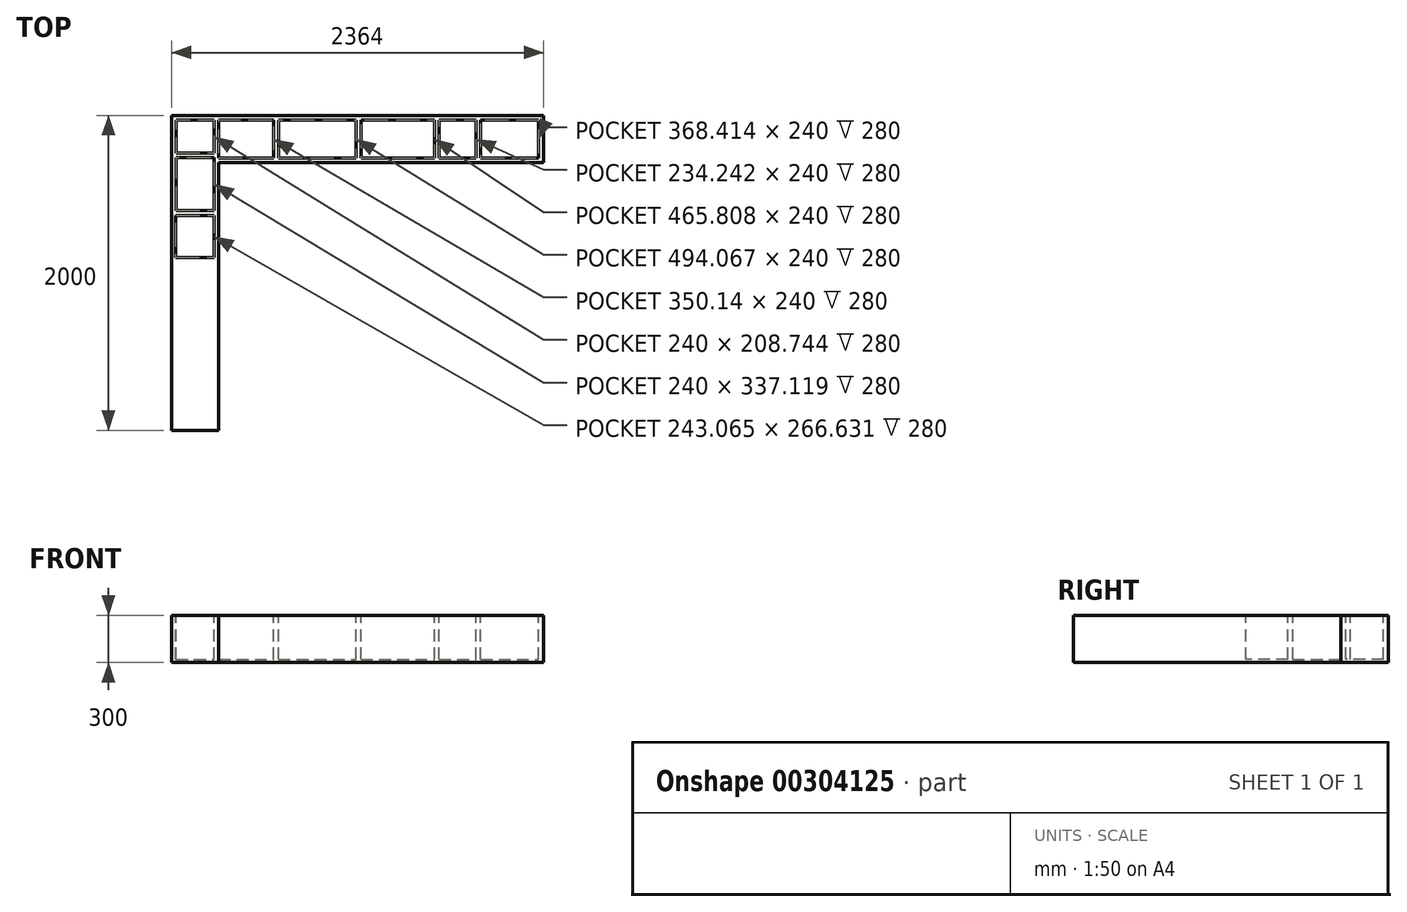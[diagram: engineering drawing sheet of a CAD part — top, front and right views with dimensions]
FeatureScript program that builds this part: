
annotation { "Feature Type Name" : "Feature", "Feature Type Description" : "" }
export const myFeature = defineFeature(function(context is Context, id is Id, definition is map)
    precondition{}
    {
        {
            var Q0;
            Q0=qCreatedBy(makeId("Top.planeOp"),FACE);
            var sketch = newSketch(context, id + "F0", { "sketchPlane" : qUnion([Q0])});
            skLineSegment(sketch, "E0.bottom", {"start": v(-1332.55, -1133.36) * mm, "end": v(-1032.55, -1133.36) * mm});
            skLineSegment(sketch, "E0.top", {"start": v(-1332.55, 866.64) * mm, "end": v(-1032.55, 866.64) * mm});
            skLineSegment(sketch, "E0.left", {"start": v(-1332.55, -1133.36) * mm, "end": v(-1332.55, 866.64) * mm});
            skLineSegment(sketch, "E0.right", {"start": v(-1032.55, -1133.36) * mm, "end": v(-1032.55, 866.64) * mm});
            skLineSegment(sketch, "E1.bottom", {"start": v(-1032.55, 866.64) * mm, "end": v(1031.45, 866.64) * mm});
            skLineSegment(sketch, "E1.top", {"start": v(-1032.55, 566.64) * mm, "end": v(1031.45, 566.64) * mm});
            skLineSegment(sketch, "E1.left", {"start": v(-1032.55, 866.64) * mm, "end": v(-1032.55, 566.64) * mm});
            skLineSegment(sketch, "E1.right", {"start": v(1031.45, 866.64) * mm, "end": v(1031.45, 566.64) * mm});
            skSolve(sketch);
        }
        {
            var Q0;
            Q0=makeQuery(id+"F0.imprint","IMPRINT",FACE,{"disambiguationData":[TD([[makeQuery(id+"F0.imprint","IMPRINT",EDGE,{"derivedFrom":sQuery(id+"F0.wireOp",EDGE,"E0.bottom")}),1.0]])]});
            var Q1;
            Q1=makeQuery(id+"F0.imprint","IMPRINT",FACE,{"disambiguationData":[TD([[makeQuery(id+"F0.imprint","IMPRINT",EDGE,{"derivedFrom":sQuery(id+"F0.wireOp",EDGE,"E1.bottom")}),-1.0]])]});
            extrude(context, id + "F1", {"entities" : qUnion([Q0, Q1]), "depth" : 300 * mm, "offsetDistance" : 25 * mm});
        }
        {
            var Q0;
            Q0=makeQuery(id+"F1.opExtrude","CAP_FACE",FACE,{"disambiguationData":[OSD([sQuery(id+"F0.wireOp",EDGE,"E0.bottom"),sQuery(id+"F0.wireOp",EDGE,"E0.top"),sQuery(id+"F0.wireOp",EDGE,"E0.left"),sQuery(id+"F0.wireOp",EDGE,"E0.right"),sQuery(id+"F0.wireOp",EDGE,"E1.bottom"),sQuery(id+"F0.wireOp",EDGE,"E1.top"),sQuery(id+"F0.wireOp",EDGE,"E1.right")])],"isStart":false});
            var sketch = newSketch(context, id + "F2", { "sketchPlane" : qUnion([Q0])});
            skLineSegment(sketch, "E2.bottom", {"start": v(-1305.62, 230.78) * mm, "end": v(-1062.55, 230.78) * mm});
            skLineSegment(sketch, "E2.top", {"start": v(-1305.62, -35.85) * mm, "end": v(-1062.55, -35.85) * mm});
            skLineSegment(sketch, "E2.left", {"start": v(-1305.62, 230.78) * mm, "end": v(-1305.62, -35.85) * mm});
            skLineSegment(sketch, "E2.right", {"start": v(-1062.55, 230.78) * mm, "end": v(-1062.55, -35.85) * mm});
            skLineSegment(sketch, "E3.bottom", {"start": v(-1062.55, 260.78) * mm, "end": v(-1302.55, 260.78) * mm});
            skLineSegment(sketch, "E3.top", {"start": v(-1062.55, 597.9) * mm, "end": v(-1302.55, 597.9) * mm});
            skLineSegment(sketch, "E3.left", {"start": v(-1062.55, 260.78) * mm, "end": v(-1062.55, 597.9) * mm});
            skLineSegment(sketch, "E3.right", {"start": v(-1302.55, 260.78) * mm, "end": v(-1302.55, 597.9) * mm});
            skLineSegment(sketch, "E4.bottom", {"start": v(-1302.55, 836.64) * mm, "end": v(-1062.55, 836.64) * mm});
            skLineSegment(sketch, "E4.top", {"start": v(-1302.55, 627.9) * mm, "end": v(-1062.55, 627.9) * mm});
            skLineSegment(sketch, "E4.left", {"start": v(-1302.55, 836.64) * mm, "end": v(-1302.55, 627.9) * mm});
            skLineSegment(sketch, "E4.right", {"start": v(-1062.55, 836.64) * mm, "end": v(-1062.55, 627.9) * mm});
            skLineSegment(sketch, "E5.top", {"start": v(-1032.55, 596.64) * mm, "end": v(-682.41, 596.64) * mm});
            skLineSegment(sketch, "E6.bottom", {"start": v(-652.41, 836.64) * mm, "end": v(-158.35, 836.64) * mm});
            skLineSegment(sketch, "E6.top", {"start": v(-652.41, 596.64) * mm, "end": v(-158.35, 596.64) * mm});
            skLineSegment(sketch, "E6.left", {"start": v(-652.41, 836.64) * mm, "end": v(-652.41, 596.64) * mm});
            skLineSegment(sketch, "E6.right", {"start": v(-158.35, 836.64) * mm, "end": v(-158.35, 596.64) * mm});
            skLineSegment(sketch, "E7.bottom", {"start": v(-128.35, 836.64) * mm, "end": v(337.46, 836.64) * mm});
            skLineSegment(sketch, "E7.top", {"start": v(-128.35, 596.64) * mm, "end": v(337.46, 596.64) * mm});
            skLineSegment(sketch, "E7.left", {"start": v(-128.35, 836.64) * mm, "end": v(-128.35, 596.64) * mm});
            skLineSegment(sketch, "E7.right", {"start": v(337.46, 836.64) * mm, "end": v(337.46, 596.64) * mm});
            skLineSegment(sketch, "E8.bottom", {"start": v(367.46, 836.64) * mm, "end": v(601.7, 836.64) * mm});
            skLineSegment(sketch, "E8.top", {"start": v(367.46, 596.64) * mm, "end": v(601.7, 596.64) * mm});
            skLineSegment(sketch, "E8.left", {"start": v(367.46, 836.64) * mm, "end": v(367.46, 596.64) * mm});
            skLineSegment(sketch, "E8.right", {"start": v(601.7, 836.64) * mm, "end": v(601.7, 596.64) * mm});
            skLineSegment(sketch, "E9.bottom", {"start": v(631.7, 836.64) * mm, "end": v(1000.12, 836.64) * mm});
            skLineSegment(sketch, "E9.top", {"start": v(631.7, 596.64) * mm, "end": v(1000.12, 596.64) * mm});
            skLineSegment(sketch, "E9.left", {"start": v(631.7, 836.64) * mm, "end": v(631.7, 596.64) * mm});
            skLineSegment(sketch, "E9.right", {"start": v(1000.12, 836.64) * mm, "end": v(1000.12, 596.64) * mm});
            skLineSegment(sketch, "E10", {"start": v(-1032.55, 596.64) * mm, "end": v(-1032.55, 836.64) * mm});
            skLineSegment(sketch, "E11", {"start": v(-1032.55, 836.64) * mm, "end": v(-682.41, 836.64) * mm});
            skLineSegment(sketch, "E12", {"start": v(-682.41, 836.64) * mm, "end": v(-682.41, 596.64) * mm});
            skSolve(sketch);
        }
        {
            var Q0;
            Q0=makeQuery(id+"F2.imprint","IMPRINT",FACE,{"disambiguationData":[TD([[makeQuery(id+"F2.imprint","IMPRINT",EDGE,{"derivedFrom":sQuery(id+"F2.wireOp",EDGE,"E2.bottom")}),-1.0]])]});
            var Q1;
            Q1=makeQuery(id+"F2.imprint","IMPRINT",FACE,{"disambiguationData":[TD([[makeQuery(id+"F2.imprint","IMPRINT",EDGE,{"derivedFrom":sQuery(id+"F2.wireOp",EDGE,"E3.bottom")}),-1.0]])]});
            var Q2;
            Q2=makeQuery(id+"F2.imprint","IMPRINT",FACE,{"disambiguationData":[TD([[makeQuery(id+"F2.imprint","IMPRINT",EDGE,{"derivedFrom":sQuery(id+"F2.wireOp",EDGE,"E4.bottom")}),-1.0]])]});
            var Q3;
            Q3=makeQuery(id+"F2.imprint","IMPRINT",FACE,{"disambiguationData":[TD([[makeQuery(id+"F2.imprint","IMPRINT",EDGE,{"derivedFrom":sQuery(id+"F2.wireOp",EDGE,"E5.top")}),1.0]])]});
            var Q4;
            Q4=makeQuery(id+"F2.imprint","IMPRINT",FACE,{"disambiguationData":[TD([[makeQuery(id+"F2.imprint","IMPRINT",EDGE,{"derivedFrom":sQuery(id+"F2.wireOp",EDGE,"E6.bottom")}),-1.0]])]});
            var Q5;
            Q5=makeQuery(id+"F2.imprint","IMPRINT",FACE,{"disambiguationData":[TD([[makeQuery(id+"F2.imprint","IMPRINT",EDGE,{"derivedFrom":sQuery(id+"F2.wireOp",EDGE,"E7.bottom")}),-1.0]])]});
            var Q6;
            Q6=makeQuery(id+"F2.imprint","IMPRINT",FACE,{"disambiguationData":[TD([[makeQuery(id+"F2.imprint","IMPRINT",EDGE,{"derivedFrom":sQuery(id+"F2.wireOp",EDGE,"E8.bottom")}),-1.0]])]});
            var Q7;
            Q7=makeQuery(id+"F2.imprint","IMPRINT",FACE,{"disambiguationData":[TD([[makeQuery(id+"F2.imprint","IMPRINT",EDGE,{"derivedFrom":sQuery(id+"F2.wireOp",EDGE,"E9.bottom")}),-1.0]])]});
            var Q8;
            Q8=makeQuery(id+"F2.imprint","IMPRINT",FACE,{"disambiguationData":[TD([[makeQuery(id+"F2.imprint","IMPRINT",EDGE,{"derivedFrom":sQuery(id+"F2.wireOp",EDGE,"f1vktL2T-XDao-MCao-i2m5-WC2OeJWGSlmK.bottom")}),-1.0]])]});
            extrude(context, id + "F3", {"entities" : qUnion([Q0, Q1, Q2, Q3, Q4, Q5, Q6, Q7, Q8]), "operationType" : NewBodyOperationType.REMOVE, "oppositeDirection" : true, "depth" : 280 * mm, "offsetDistance" : 25 * mm});
        }
    });
